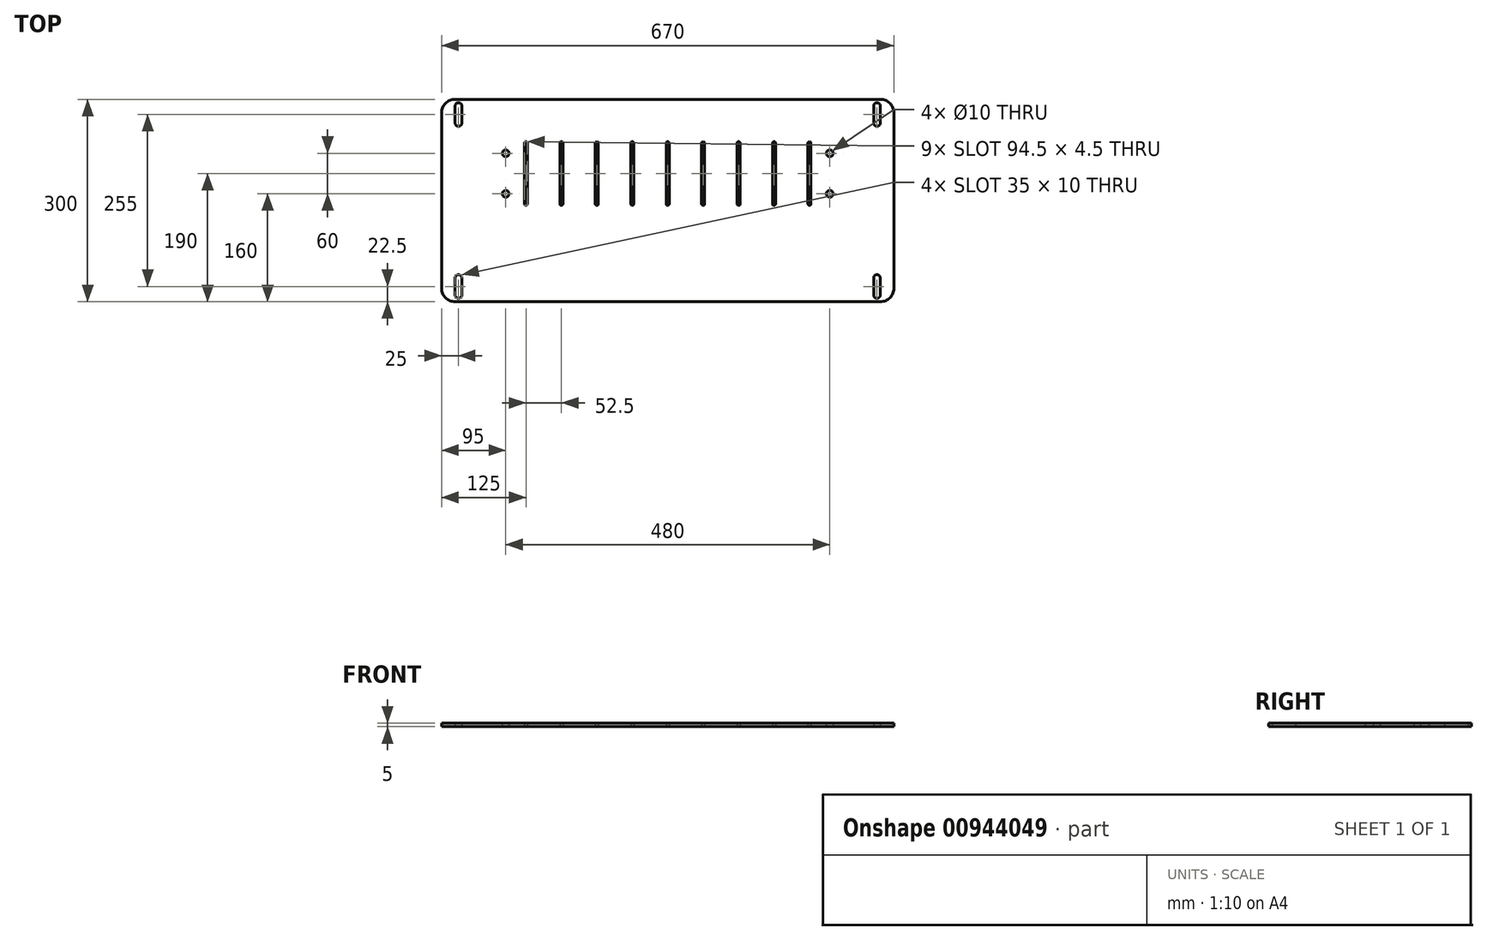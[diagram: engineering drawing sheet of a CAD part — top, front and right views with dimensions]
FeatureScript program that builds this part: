
annotation { "Feature Type Name" : "Feature", "Feature Type Description" : "" }
export const myFeature = defineFeature(function(context is Context, id is Id, definition is map)
    precondition{}
    {
        {
            var Q0;
            Q0=qCreatedBy(makeId("Top.planeOp"),FACE);
            var sketch = newSketch(context, id + "F0", { "sketchPlane" : qUnion([Q0])});
            skLineSegment(sketch, "E0.bottom", {"start": v(-315, 150) * mm, "end": v(315, 150) * mm});
            skLineSegment(sketch, "E0.top", {"start": v(-315, -150) * mm, "end": v(315, -150) * mm});
            skLineSegment(sketch, "E0.left", {"start": v(-335, 130) * mm, "end": v(-335, -130) * mm});
            skLineSegment(sketch, "E0.right", {"start": v(335, 130) * mm, "end": v(335, -130) * mm});
            skPoint(sketch, "E0.middle", {"position": v(0, 0) * mm});
            skPoint(sketch, "E1.visualSharp", {"position": v(-335, 150) * mm});
            skArc(sketch, "E1.filletArc", {"start": v(-315, 150) * mm, "mid": v(-329.14, 144.14) * mm, "end": v(-335, 130) * mm});
            skPoint(sketch, "E2.visualSharp", {"position": v(-335, -150) * mm});
            skArc(sketch, "E2.filletArc", {"start": v(-335, -130) * mm, "mid": v(-329.14, -144.14) * mm, "end": v(-315, -150) * mm});
            skPoint(sketch, "E3.visualSharp", {"position": v(335, -150) * mm});
            skArc(sketch, "E3.filletArc", {"start": v(315, -150) * mm, "mid": v(329.14, -144.14) * mm, "end": v(335, -130) * mm});
            skPoint(sketch, "E4.visualSharp", {"position": v(335, 150) * mm});
            skArc(sketch, "E4.filletArc", {"start": v(335, 130) * mm, "mid": v(329.14, 144.14) * mm, "end": v(315, 150) * mm});
            skArc(sketch, "E5", {"start": v(-305, 140) * mm, "mid": v(-310, 145) * mm, "end": v(-315, 140) * mm});
            skArc(sketch, "E6", {"start": v(-315, 115) * mm, "mid": v(-310, 110) * mm, "end": v(-305, 115) * mm});
            skLineSegment(sketch, "E7", {"start": v(-305, 140) * mm, "end": v(-305, 115) * mm});
            skLineSegment(sketch, "E8", {"start": v(-315, 115) * mm, "end": v(-315, 140) * mm});
            skLineSegment(sketch, "E9", {"start": v(0, 0) * mm, "end": v(0, 123.18) * mm, "construction": true});
            skArc(sketch, "E10.MirrorCS", {"start": v(315, 115) * mm, "mid": v(310, 110) * mm, "end": v(305, 115) * mm});
            skLineSegment(sketch, "E11.MirrorCS", {"start": v(305, 140) * mm, "end": v(305, 115) * mm});
            skLineSegment(sketch, "E12.MirrorCS", {"start": v(315, 115) * mm, "end": v(315, 140) * mm});
            skArc(sketch, "E13.MirrorCS", {"start": v(305, 140) * mm, "mid": v(310, 145) * mm, "end": v(315, 140) * mm});
            skLineSegment(sketch, "E14", {"start": v(0, 0) * mm, "end": v(264.77, 0) * mm, "construction": true});
            skArc(sketch, "E15.MirrorCS", {"start": v(315, -115) * mm, "mid": v(310, -110) * mm, "end": v(305, -115) * mm});
            skLineSegment(sketch, "E16.MirrorCS", {"start": v(315, -115) * mm, "end": v(315, -140) * mm});
            skArc(sketch, "E17.MirrorCS", {"start": v(305, -140) * mm, "mid": v(310, -145) * mm, "end": v(315, -140) * mm});
            skLineSegment(sketch, "E18.MirrorCS", {"start": v(305, -140) * mm, "end": v(305, -115) * mm});
            skArc(sketch, "E19.MirrorCS", {"start": v(-315, -115) * mm, "mid": v(-310, -110) * mm, "end": v(-305, -115) * mm});
            skLineSegment(sketch, "E20.MirrorCS", {"start": v(-305, -140) * mm, "end": v(-305, -115) * mm});
            skLineSegment(sketch, "E21.MirrorCS", {"start": v(-315, -115) * mm, "end": v(-315, -140) * mm});
            skArc(sketch, "E22.MirrorCS", {"start": v(-305, -140) * mm, "mid": v(-310, -145) * mm, "end": v(-315, -140) * mm});
            skCircle(sketch, "E23", {"center": v(-240, 70) * mm, "radius": 5 * mm});
            skCircle(sketch, "E24", {"center": v(-240, 10) * mm, "radius": 5 * mm});
            skCircle(sketch, "E25.MirrorC", {"center": v(240, 70) * mm, "radius": 5 * mm});
            skCircle(sketch, "E26.MirrorC", {"center": v(240, 10) * mm, "radius": 5 * mm});
            skArc(sketch, "E27", {"start": v(-212.25, -5) * mm, "mid": v(-210, -7.25) * mm, "end": v(-207.75, -5) * mm});
            skArc(sketch, "E28", {"start": v(-207.75, 85) * mm, "mid": v(-210, 87.25) * mm, "end": v(-212.25, 85) * mm});
            skLineSegment(sketch, "E29", {"start": v(-210, 85) * mm, "end": v(-207.75, 85) * mm});
            skLineSegment(sketch, "E30", {"start": v(-207.75, 85) * mm, "end": v(-207.75, -5) * mm});
            skLineSegment(sketch, "E31", {"start": v(-212.25, -5) * mm, "end": v(-212.25, 85) * mm});
            skLineSegment(sketch, "E32.1.0.0", {"start": v(-155.25, 85) * mm, "end": v(-155.25, -5) * mm});
            skArc(sketch, "E32.1.0.1", {"start": v(-155.25, 85) * mm, "mid": v(-157.5, 87.25) * mm, "end": v(-159.75, 85) * mm});
            skLineSegment(sketch, "E32.1.0.2", {"start": v(-159.75, -5) * mm, "end": v(-159.75, 85) * mm});
            skArc(sketch, "E32.1.0.3", {"start": v(-159.75, -5) * mm, "mid": v(-157.5, -7.25) * mm, "end": v(-155.25, -5) * mm});
            skLineSegment(sketch, "E32.2.0.0", {"start": v(-102.75, 85) * mm, "end": v(-102.75, -5) * mm});
            skArc(sketch, "E32.2.0.1", {"start": v(-102.75, 85) * mm, "mid": v(-105, 87.25) * mm, "end": v(-107.25, 85) * mm});
            skLineSegment(sketch, "E32.2.0.2", {"start": v(-107.25, -5) * mm, "end": v(-107.25, 85) * mm});
            skArc(sketch, "E32.2.0.3", {"start": v(-107.25, -5) * mm, "mid": v(-105, -7.25) * mm, "end": v(-102.75, -5) * mm});
            skLineSegment(sketch, "E32.3.0.0", {"start": v(-50.25, 85) * mm, "end": v(-50.25, -5) * mm});
            skArc(sketch, "E32.3.0.1", {"start": v(-50.25, 85) * mm, "mid": v(-52.5, 87.25) * mm, "end": v(-54.75, 85) * mm});
            skLineSegment(sketch, "E32.3.0.2", {"start": v(-54.75, -5) * mm, "end": v(-54.75, 85) * mm});
            skArc(sketch, "E32.3.0.3", {"start": v(-54.75, -5) * mm, "mid": v(-52.5, -7.25) * mm, "end": v(-50.25, -5) * mm});
            skLineSegment(sketch, "E32.4.0.0", {"start": v(2.25, 85) * mm, "end": v(2.25, -5) * mm});
            skArc(sketch, "E32.4.0.1", {"start": v(2.25, 85) * mm, "mid": v(0, 87.25) * mm, "end": v(-2.25, 85) * mm});
            skLineSegment(sketch, "E32.4.0.2", {"start": v(-2.25, -5) * mm, "end": v(-2.25, 85) * mm});
            skArc(sketch, "E32.4.0.3", {"start": v(-2.25, -5) * mm, "mid": v(0, -7.25) * mm, "end": v(2.25, -5) * mm});
            skLineSegment(sketch, "E32.5.0.0", {"start": v(54.75, 85) * mm, "end": v(54.75, -5) * mm});
            skArc(sketch, "E32.5.0.1", {"start": v(54.75, 85) * mm, "mid": v(52.5, 87.25) * mm, "end": v(50.25, 85) * mm});
            skLineSegment(sketch, "E32.5.0.2", {"start": v(50.25, -5) * mm, "end": v(50.25, 85) * mm});
            skArc(sketch, "E32.5.0.3", {"start": v(50.25, -5) * mm, "mid": v(52.5, -7.25) * mm, "end": v(54.75, -5) * mm});
            skLineSegment(sketch, "E32.6.0.0", {"start": v(107.25, 85) * mm, "end": v(107.25, -5) * mm});
            skArc(sketch, "E32.6.0.1", {"start": v(107.25, 85) * mm, "mid": v(105, 87.25) * mm, "end": v(102.75, 85) * mm});
            skLineSegment(sketch, "E32.6.0.2", {"start": v(102.75, -5) * mm, "end": v(102.75, 85) * mm});
            skArc(sketch, "E32.6.0.3", {"start": v(102.75, -5) * mm, "mid": v(105, -7.25) * mm, "end": v(107.25, -5) * mm});
            skLineSegment(sketch, "E32.7.0.0", {"start": v(159.75, 85) * mm, "end": v(159.75, -5) * mm});
            skArc(sketch, "E32.7.0.1", {"start": v(159.75, 85) * mm, "mid": v(157.5, 87.25) * mm, "end": v(155.25, 85) * mm});
            skLineSegment(sketch, "E32.7.0.2", {"start": v(155.25, -5) * mm, "end": v(155.25, 85) * mm});
            skArc(sketch, "E32.7.0.3", {"start": v(155.25, -5) * mm, "mid": v(157.5, -7.25) * mm, "end": v(159.75, -5) * mm});
            skLineSegment(sketch, "E32.8.0.0", {"start": v(212.25, 85) * mm, "end": v(212.25, -5) * mm});
            skArc(sketch, "E32.8.0.1", {"start": v(212.25, 85) * mm, "mid": v(210, 87.25) * mm, "end": v(207.75, 85) * mm});
            skLineSegment(sketch, "E32.8.0.2", {"start": v(207.75, -5) * mm, "end": v(207.75, 85) * mm});
            skArc(sketch, "E32.8.0.3", {"start": v(207.75, -5) * mm, "mid": v(210, -7.25) * mm, "end": v(212.25, -5) * mm});
            skLineSegment(sketch, "E32.direction1", {"start": v(-207.75, -5) * mm, "end": v(-155.25, -5) * mm, "construction": true});
            skSolve(sketch);
        }
        {
            var Q0;
            Q0=makeQuery(id+"F0.imprint","IMPRINT",FACE,{"disambiguationData":[TD([[makeQuery(id+"F0.imprint","IMPRINT",EDGE,{"derivedFrom":sQuery(id+"F0.wireOp",EDGE,"E0.bottom")}),-1.0]])]});
            extrude(context, id + "F1", {"entities" : qUnion([Q0]), "depth" : 5 * mm, "offsetDistance" : 25 * mm});
        }
    });
